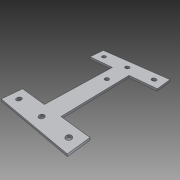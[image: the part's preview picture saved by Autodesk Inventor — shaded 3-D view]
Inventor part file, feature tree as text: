
AUTODESK INVENTOR PART (.ipt)
format: ipt  version: 2014 SP1 (Build 180222100, 222)  size: 102,912 bytes
history: native  units: in
note: dims shown in document units (in); Inventor stores cm internally (conversion verified against a paired STEP export)
features: extrude x1, sketch x1, reference x1
ambient origin geometry x8: Origin, YZ Plane, XZ Plane, XY Plane, X Axis, Y Axis, Z Axis, Center Point
bodies: Solid1 (feature_tree)
feature tree (3):
  extrude  "Extrusion1"  Depth=4.0in
  sketch  "Sketch1"  dims[d0=1.0in d1=4.0in d4=1.5in d5=0.266in d6=0.5in d7=1.1811in d9=1.5in d10=0.7874in d12=5.0in d15=6.0in d16=1.0in d17=0.75in d18=0.125in d19=0.0in d20=0.9438in]
  reference  "Reference1"
